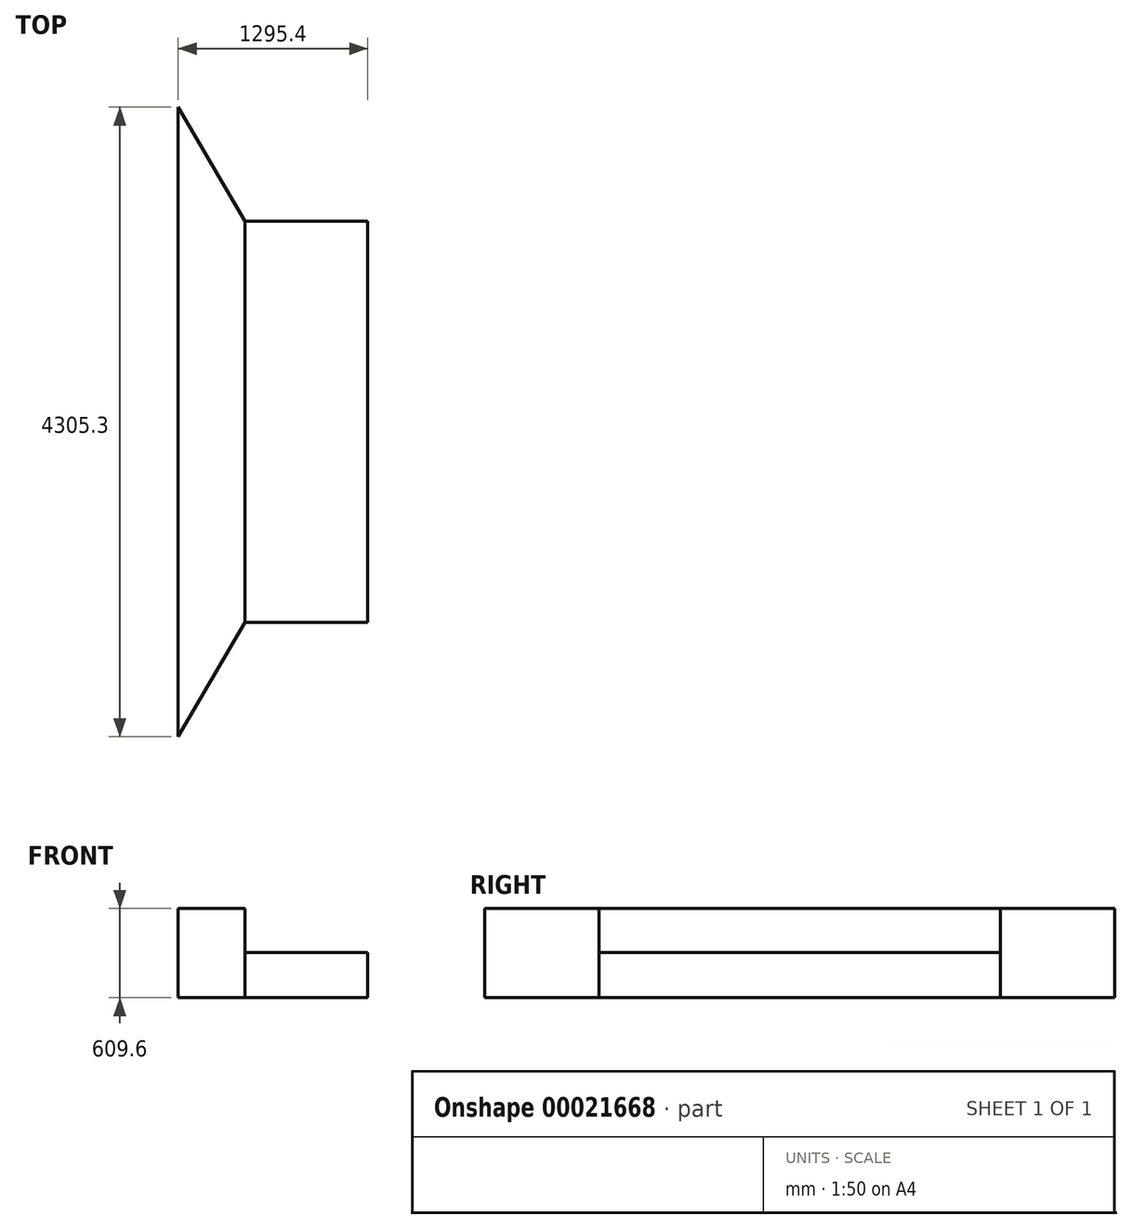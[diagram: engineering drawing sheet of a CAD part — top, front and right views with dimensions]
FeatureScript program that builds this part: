
annotation { "Feature Type Name" : "Feature", "Feature Type Description" : "" }
export const myFeature = defineFeature(function(context is Context, id is Id, definition is map)
    precondition{}
    {
        {
            var Q0;
            Q0=qCreatedBy(makeId("Top.planeOp"),FACE);
            var sketch = newSketch(context, id + "F0", { "sketchPlane" : qUnion([Q0])});
            skLineSegment(sketch, "E0.rect.bottom", {"start": v(54.73, 32.01) * mm, "end": v(-54.73, 32.01) * mm, "construction": true});
            skLineSegment(sketch, "E0.rect.top", {"start": v(54.73, -32.01) * mm, "end": v(-54.73, -32.01) * mm, "construction": true});
            skLineSegment(sketch, "E0.rect.left", {"start": v(54.73, 32.01) * mm, "end": v(54.73, -32.01) * mm, "construction": true});
            skLineSegment(sketch, "E0.rect.right", {"start": v(-54.73, 32.01) * mm, "end": v(-54.73, -32.01) * mm, "construction": true});
            skPoint(sketch, "E0.rect.middle", {"position": v(0, 0) * mm});
            skSolve(sketch);
        }
        {
            var Q0;
            Q0=qCreatedBy(makeId("Top.planeOp"),FACE);
            var sketch = newSketch(context, id + "F1", { "sketchPlane" : qUnion([Q0])});
            skLineSegment(sketch, "E1", {"start": v(0, 0) * mm, "end": v(0, -4305.3) * mm});
            skLineSegment(sketch, "E2", {"start": v(0, -4305.3) * mm, "end": v(457.2, -3524.25) * mm});
            skLineSegment(sketch, "E3", {"start": v(457.2, -3524.25) * mm, "end": v(457.2, -781.05) * mm});
            skLineSegment(sketch, "E4", {"start": v(457.2, -781.05) * mm, "end": v(0, 0) * mm});
            skLineSegment(sketch, "E5.left", {"start": v(457.2, -781.05) * mm, "end": v(457.2, -3524.25) * mm});
            skSolve(sketch);
        }
        {
            var Q0;
            Q0=qCreatedBy(makeId("Top.planeOp"),FACE);
            var sketch = newSketch(context, id + "F2", { "sketchPlane" : qUnion([Q0])});
            skLineSegment(sketch, "E6.bottom", {"start": v(457.2, -781.05) * mm, "end": v(1295.4, -781.05) * mm});
            skLineSegment(sketch, "E6.top", {"start": v(457.2, -3524.25) * mm, "end": v(1295.4, -3524.25) * mm});
            skLineSegment(sketch, "E6.left", {"start": v(457.2, -781.05) * mm, "end": v(457.2, -3524.25) * mm});
            skLineSegment(sketch, "E6.right", {"start": v(1295.4, -781.05) * mm, "end": v(1295.4, -3524.25) * mm});
            skSolve(sketch);
        }
        {
            var Q0;
            Q0=makeQuery(id+"F1.imprint","IMPRINT",FACE,{"disambiguationData":[TD([[makeQuery(id+"F1.imprint","IMPRINT",EDGE,{"derivedFrom":sQuery(id+"F1.wireOp",EDGE,"E1")}),1.0]])]});
            extrude(context, id + "F3", {"entities" : qUnion([Q0]), "depth" : 609.6 * mm});
        }
        {
            var Q0;
            Q0=makeQuery(id+"F2.imprint","IMPRINT",FACE,{"disambiguationData":[TD([[makeQuery(id+"F2.imprint","IMPRINT",EDGE,{"derivedFrom":sQuery(id+"F2.wireOp",EDGE,"E6.bottom")}),-1.0]])]});
            extrude(context, id + "F4", {"entities" : qUnion([Q0]), "operationType" : NewBodyOperationType.ADD, "depth" : 309.56 * mm});
        }
        {
            var Q0;
            Q0=makeQuery(id+"F4.opExtrude","CAP_FACE",FACE,{"disambiguationData":[OSD([sQuery(id+"F2.wireOp",EDGE,"E6.bottom"),sQuery(id+"F2.wireOp",EDGE,"E6.top"),sQuery(id+"F2.wireOp",EDGE,"E6.left"),sQuery(id+"F2.wireOp",EDGE,"E6.right")])],"isStart":false});
            var sketch = newSketch(context, id + "F5", { "sketchPlane" : qUnion([Q0])});
            skLineSegment(sketch, "E7", {"start": v(457.2, -1085.85) * mm, "end": v(1295.4, -1085.85) * mm, "construction": true});
            skLineSegment(sketch, "E8", {"start": v(457.2, -3219.45) * mm, "end": v(1295.4, -3219.45) * mm, "construction": true});
            skPoint(sketch, "E9", {"position": v(457.2, -3219.45) * mm});
            skPoint(sketch, "E10", {"position": v(457.2, -1085.85) * mm});
            skSolve(sketch);
        }
    });
